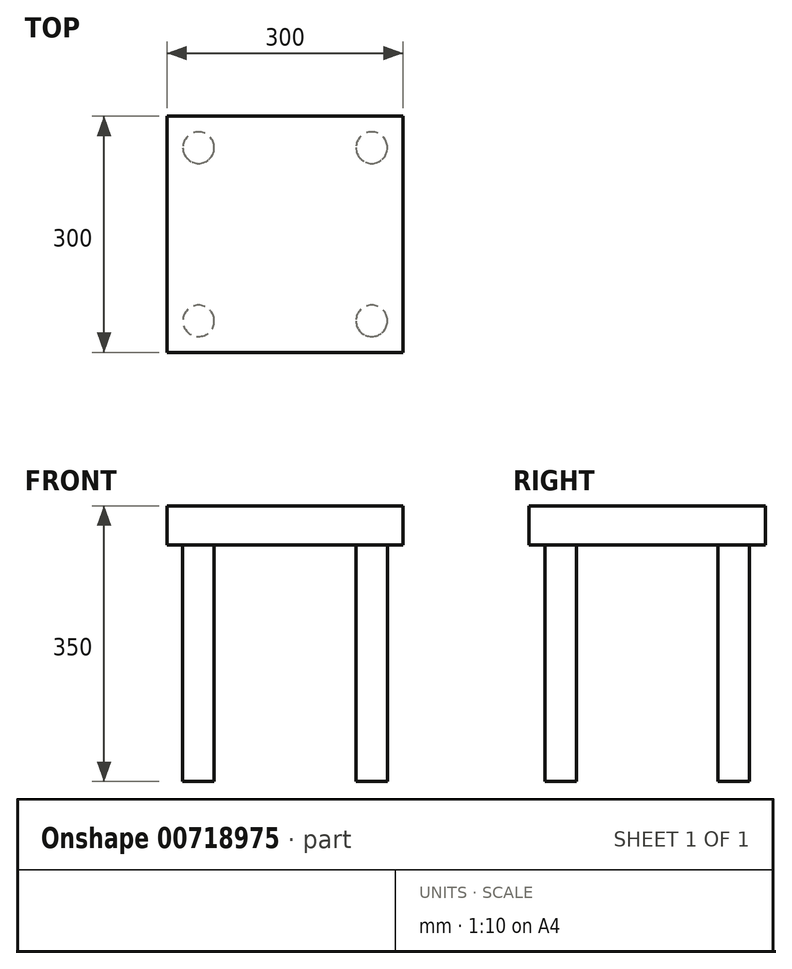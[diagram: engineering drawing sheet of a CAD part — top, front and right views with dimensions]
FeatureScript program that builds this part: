
annotation { "Feature Type Name" : "Feature", "Feature Type Description" : "" }
export const myFeature = defineFeature(function(context is Context, id is Id, definition is map)
    precondition{}
    {
        {
            var Q0;
            Q0=qCreatedBy(makeId("Front.planeOp"),FACE);
            var sketch = newSketch(context, id + "F0", { "sketchPlane" : qUnion([Q0])});
            skLineSegment(sketch, "E0.bottom", {"start": v(-150, 400) * mm, "end": v(150, 400) * mm});
            skLineSegment(sketch, "E0.top", {"start": v(-150, 350) * mm, "end": v(150, 350) * mm});
            skLineSegment(sketch, "E0.left", {"start": v(-150, 400) * mm, "end": v(-150, 350) * mm});
            skLineSegment(sketch, "E0.right", {"start": v(150, 400) * mm, "end": v(150, 350) * mm});
            skLineSegment(sketch, "E1.bottom", {"start": v(-150, 350) * mm, "end": v(-130, 350) * mm});
            skLineSegment(sketch, "E1.top", {"start": v(-150, 0) * mm, "end": v(-130, 0) * mm});
            skLineSegment(sketch, "E1.left", {"start": v(-150, 350) * mm, "end": v(-150, 0) * mm});
            skLineSegment(sketch, "E1.right", {"start": v(-130, 350) * mm, "end": v(-130, 0) * mm});
            skSolve(sketch);
        }
        {
            var Q0;
            Q0=makeQuery(id+"F0.imprint","IMPRINT",FACE,{"disambiguationData":[TD([[makeQuery(id+"F0.imprint","IMPRINT",EDGE,{"derivedFrom":sQuery(id+"F0.wireOp",EDGE,"E0.bottom")}),-1.0]])]});
            extrude(context, id + "F1", {"entities" : qUnion([Q0]), "endBound" : BoundingType.SYMMETRIC, "depth" : 300 * mm, "offsetDistance" : 25 * mm});
        }
        {
            var Q0;
            Q0=makeQuery(id+"F1.opExtrude","SWEPT_FACE",FACE,{"disambiguationData":[OSD([sQuery(id+"F0.wireOp",EDGE,"E0.top"),sQuery(id+"F0.wireOp",EDGE,"E1.bottom")])]});
            var sketch = newSketch(context, id + "F2", { "sketchPlane" : qUnion([Q0])});
            skCircle(sketch, "E2", {"center": v(-110, 110) * mm, "radius": 20 * mm});
            skCircle(sketch, "E3.0.1.0", {"center": v(-110, -110) * mm, "radius": 20 * mm});
            skCircle(sketch, "E3.1.0.0", {"center": v(110, 110) * mm, "radius": 20 * mm});
            skCircle(sketch, "E3.1.1.0", {"center": v(110, -110) * mm, "radius": 20 * mm});
            skLineSegment(sketch, "E3.direction1", {"start": v(-110, 110) * mm, "end": v(110, 110) * mm, "construction": true});
            skLineSegment(sketch, "E3.direction2", {"start": v(-110, 110) * mm, "end": v(-110, -110) * mm, "construction": true});
            skSolve(sketch);
        }
        {
            var Q0;
            Q0=makeQuery(id+"F2.imprint","IMPRINT",FACE,{"disambiguationData":[TD([[makeQuery(id+"F2.imprint","IMPRINT",EDGE,{"derivedFrom":sQuery(id+"F2.wireOp",EDGE,"E3.1.0.0")}),1.0]])]});
            var Q1;
            Q1=makeQuery(id+"F2.imprint","IMPRINT",FACE,{"disambiguationData":[TD([[makeQuery(id+"F2.imprint","IMPRINT",EDGE,{"derivedFrom":sQuery(id+"F2.wireOp",EDGE,"E2")}),1.0]])]});
            var Q2;
            Q2=makeQuery(id+"F2.imprint","IMPRINT",FACE,{"disambiguationData":[TD([[makeQuery(id+"F2.imprint","IMPRINT",EDGE,{"derivedFrom":sQuery(id+"F2.wireOp",EDGE,"E3.0.1.0")}),1.0]])]});
            var Q3;
            Q3=makeQuery(id+"F2.imprint","IMPRINT",FACE,{"disambiguationData":[TD([[makeQuery(id+"F2.imprint","IMPRINT",EDGE,{"derivedFrom":sQuery(id+"F2.wireOp",EDGE,"E3.1.1.0")}),1.0]])]});
            extrude(context, id + "F3", {"entities" : qUnion([Q0, Q1, Q2, Q3]), "operationType" : NewBodyOperationType.ADD, "depth" : 300 * mm, "offsetDistance" : 25 * mm});
        }
    });
